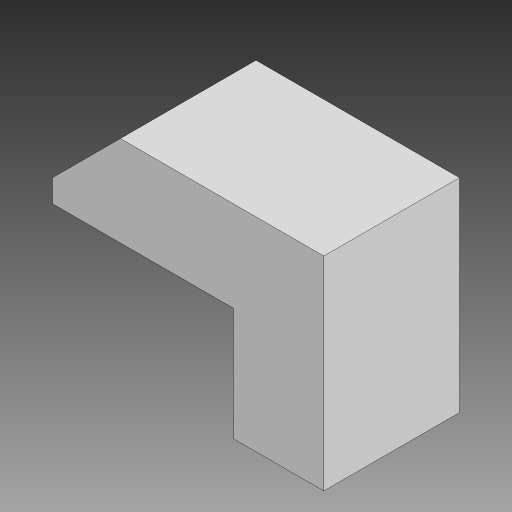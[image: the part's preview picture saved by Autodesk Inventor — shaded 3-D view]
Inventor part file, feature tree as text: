
AUTODESK INVENTOR PART (.ipt)
format: ipt  version: 2023 (Build 270158000, 158)  size: 227,840 bytes
history: native  units: mm
features: other x1, extrude x1, chamfer x1, sketch x1
ambient origin geometry x8: Origin, YZ Plane, XZ Plane, XY Plane, X Axis, Y Axis, Z Axis, Center Point
bodies: Body1 (feature_tree)
feature tree (4):
  other  "Těleso1"
  extrude  "Vysunutí1"  Depth=6.0mm
  chamfer  "Zkosení1"  Distance=2.0mm
  sketch  "Náčrt1"
